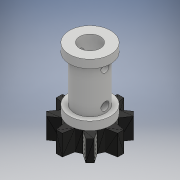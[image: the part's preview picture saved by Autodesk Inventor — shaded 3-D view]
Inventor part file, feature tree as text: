
AUTODESK INVENTOR PART (.ipt)
format: ipt  version: 2018 (Build 220112000, 112)  size: 181,760 bytes
history: native  units: mm
features: extrude x7, sketch x7, other x3
ambient origin geometry x8: Origin, YZ Plane, XZ Plane, XY Plane, X Axis, Y Axis, Z Axis, Center Point
bodies: Body1 (feature_tree)
feature tree (17):
  other  "eng_chic_2_1"
  other  "Sólido1"
  extrude  "Extrusión1"  Depth=7.5mm
  extrude  "Extrusión2"  Depth=2.0mm TaperAngle=0.0deg
  extrude  "Extrusión3"  Depth=22.0mm TaperAngle=0.0deg
  extrude  "Extrusión4"  Depth=1.5mm
  extrude  "Extrusión5"  Depth=2.0mm
  extrude  "Extrusión6"  Depth=5.0mm TaperAngle=0.0deg
  extrude  "Extrusión7"  [1 undecoded]
  sketch  "Boceto1"  dims[d0=2.0mm d1=0.0mm d2=7.5mm]
  sketch  "Boceto2"  dims[d3=11.0mm d4=0.0mm d5=2.0mm d6=0.0mm]
  sketch  "Boceto3"  dims[d7=5.0mm d8=22.0mm d9=0.0mm]
  sketch  "Boceto4"  dims[d10=1.5mm d11=1.5mm]
  sketch  "Boceto5"  dims[d12=2.0mm d13=2.0mm]
  sketch  "Boceto7"  dims[d14=22.0mm d15=0.0mm d16=5.0mm d17=0.0mm]
  sketch  "Boceto8"  dims[d18=5.0mm d19=0.0mm]
  other  "MeshFeature1"
note: 1 required parameter value undecoded (feature->parameter linkage not recoverable at this tier; creation-order binding heuristic only, values carry confidence <= 0.55)
